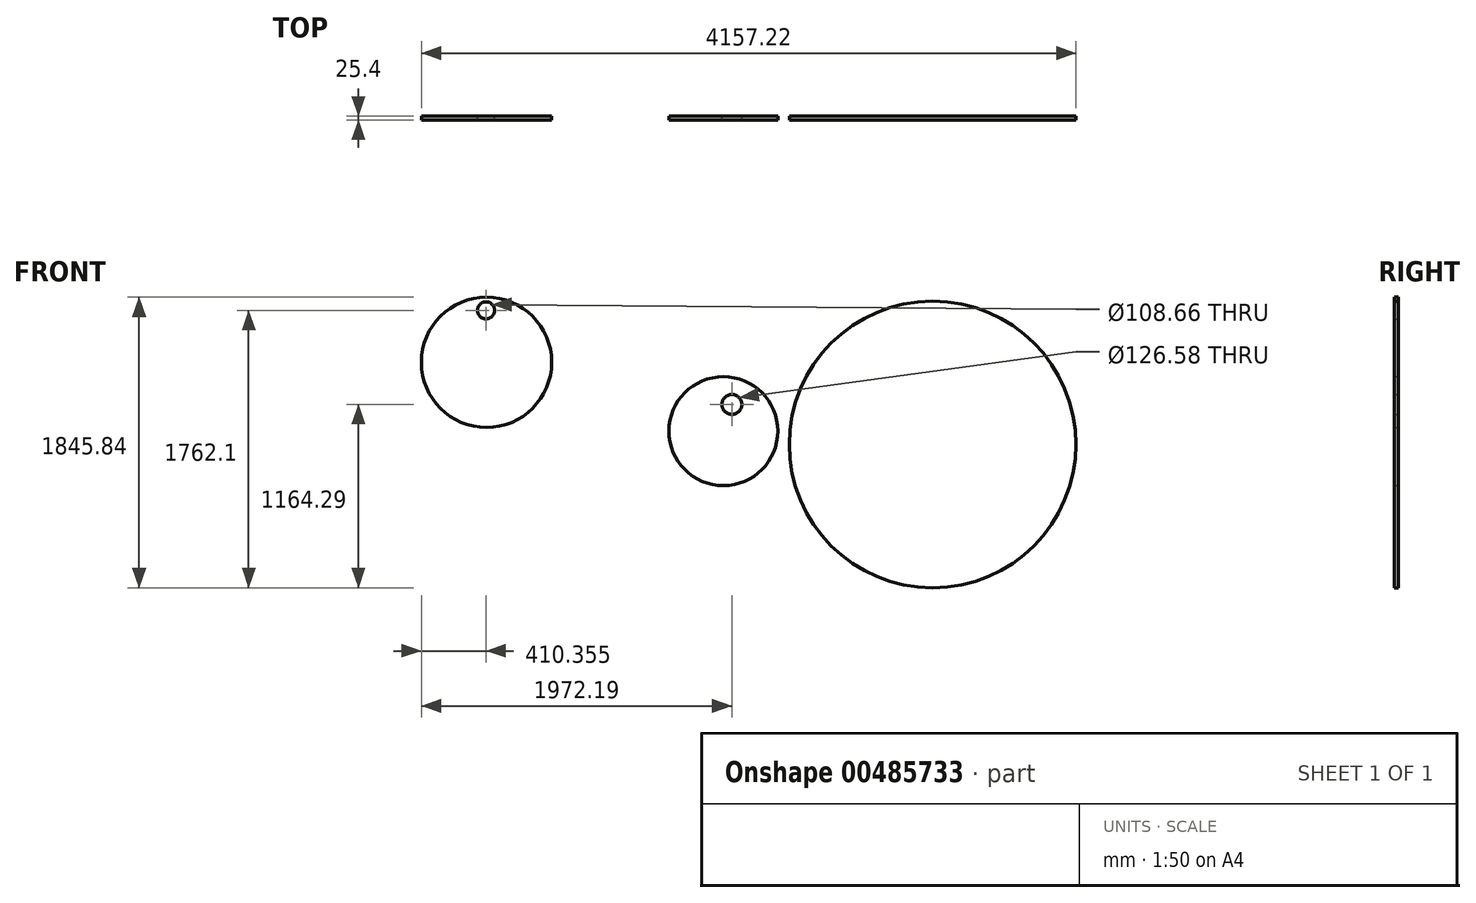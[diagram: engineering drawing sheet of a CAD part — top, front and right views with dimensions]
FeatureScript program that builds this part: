
annotation { "Feature Type Name" : "Feature", "Feature Type Description" : "" }
export const myFeature = defineFeature(function(context is Context, id is Id, definition is map)
    precondition{}
    {
        {
            var Q0;
            Q0=qCreatedBy(makeId("Front.planeOp"),FACE);
            var sketch = newSketch(context, id + "F0", { "sketchPlane" : qUnion([Q0])});
            skCircle(sketch, "E0", {"center": v(-559.4, 956.92) * mm, "radius": 413.7 * mm});
            skCircle(sketch, "E1", {"center": v(944.84, 519.46) * mm, "radius": 345.83 * mm});
            skCircle(sketch, "E2", {"center": v(2273.7, 435.2) * mm, "radius": 910.42 * mm});
            skCircle(sketch, "E3", {"center": v(-562.75, 1286.89) * mm, "radius": 54.33 * mm});
            skCircle(sketch, "E4", {"center": v(758.84, 731.38) * mm, "radius": 63.87 * mm});
            skCircle(sketch, "E5", {"center": v(999.1, 689.08) * mm, "radius": 63.29 * mm});
            skSolve(sketch);
        }
        {
            var Q0;
            Q0 = qSketchRegion(id + "F0", true);
            extrude(context, id + "F1", {"entities" : qUnion([Q0]), "depth" : 25.4 * mm});
        }
    });
